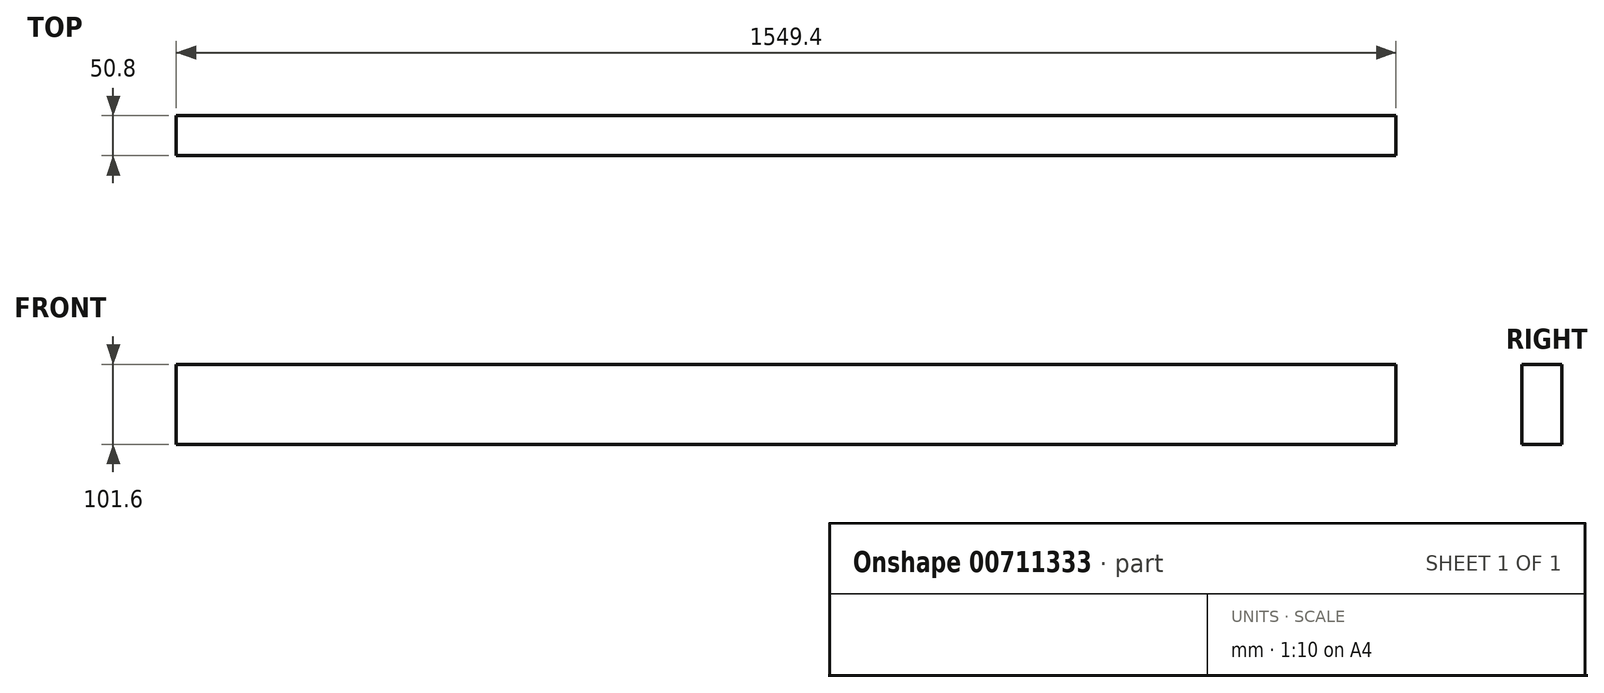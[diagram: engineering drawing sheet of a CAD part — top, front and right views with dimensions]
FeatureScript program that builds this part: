
annotation { "Feature Type Name" : "Feature", "Feature Type Description" : "" }
export const myFeature = defineFeature(function(context is Context, id is Id, definition is map)
    precondition{}
    {
        {
            var Q0;
            Q0=qCreatedBy(makeId("Right.planeOp"),FACE);
            var sketch = newSketch(context, id + "F0", { "sketchPlane" : qUnion([Q0])});
            skLineSegment(sketch, "E0.bottom", {"start": v(25.4, 50.8) * mm, "end": v(-25.4, 50.8) * mm});
            skLineSegment(sketch, "E0.top", {"start": v(25.4, -50.8) * mm, "end": v(-25.4, -50.8) * mm});
            skLineSegment(sketch, "E0.left", {"start": v(25.4, 50.8) * mm, "end": v(25.4, -50.8) * mm});
            skLineSegment(sketch, "E0.right", {"start": v(-25.4, 50.8) * mm, "end": v(-25.4, -50.8) * mm});
            skPoint(sketch, "E0.middle", {"position": v(0, 0) * mm});
            skSolve(sketch);
        }
        {
            var Q0;
            Q0 = qSketchRegion(id + "F0", true);
            extrude(context, id + "F1", {"entities" : qUnion([Q0]), "depth" : 1549.4 * mm, "offsetDistance" : 25.4 * mm});
        }
    });
